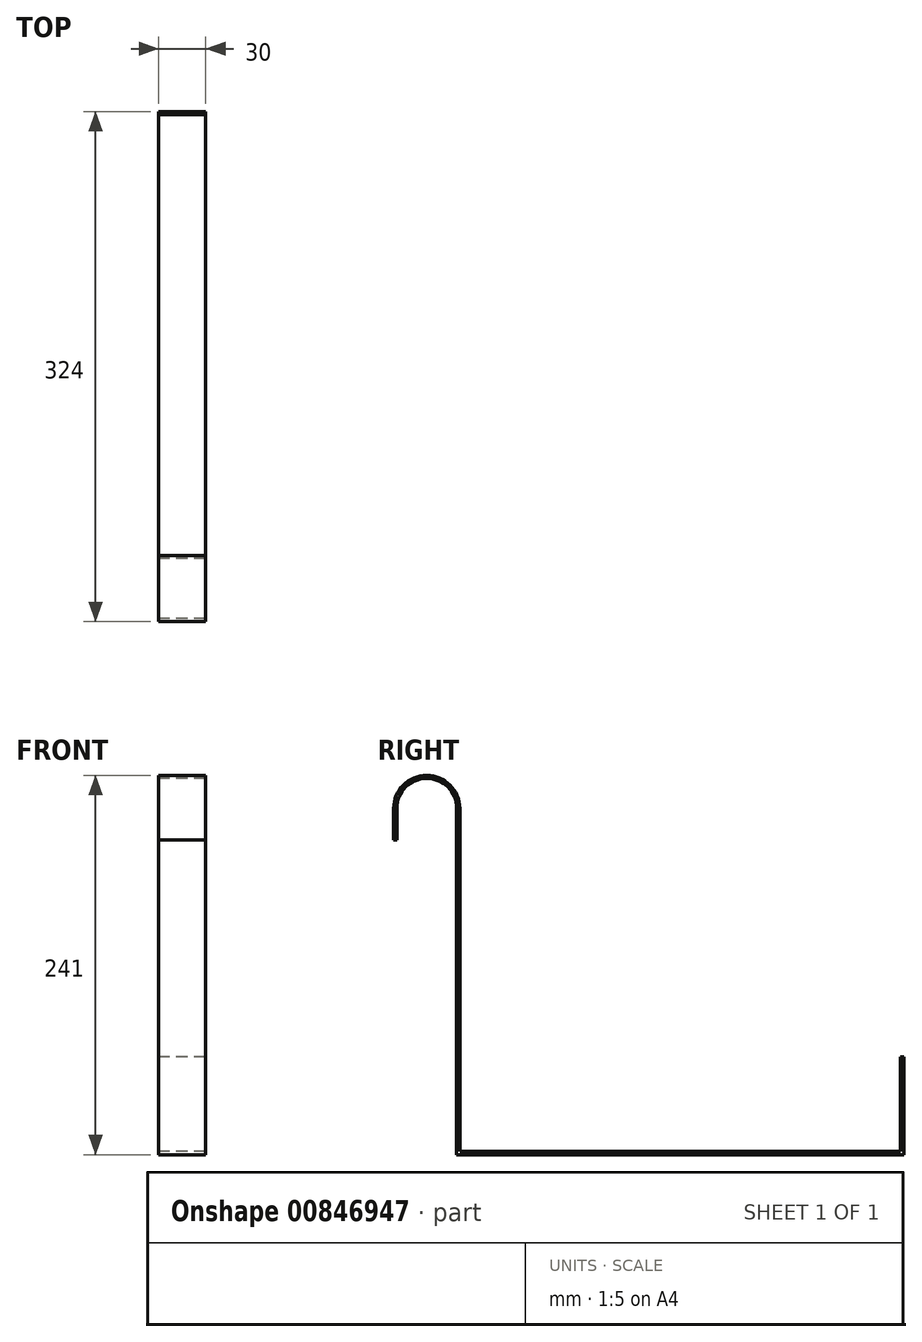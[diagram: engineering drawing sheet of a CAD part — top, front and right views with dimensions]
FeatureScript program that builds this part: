
annotation { "Feature Type Name" : "Feature", "Feature Type Description" : "" }
export const myFeature = defineFeature(function(context is Context, id is Id, definition is map)
    precondition{}
    {
        {
            var Q0;
            Q0=qCreatedBy(makeId("Right.planeOp"),FACE);
            var sketch = newSketch(context, id + "F0", { "sketchPlane" : qUnion([Q0])});
            skArc(sketch, "E0", {"start": v(19, 220) * mm, "mid": v(0, 239) * mm, "end": v(-19, 220) * mm});
            skLineSegment(sketch, "E1", {"start": v(0, 220) * mm, "end": v(19, 220) * mm, "construction": true});
            skLineSegment(sketch, "E2", {"start": v(19, 220) * mm, "end": v(19, 0) * mm});
            skLineSegment(sketch, "E3", {"start": v(0, 220) * mm, "end": v(-19, 220) * mm, "construction": true});
            skArc(sketch, "E4.0", {"start": v(21, 220) * mm, "mid": v(0, 241) * mm, "end": v(-21, 220) * mm});
            skLineSegment(sketch, "E4.1", {"start": v(21, 220) * mm, "end": v(21, 0) * mm});
            skLineSegment(sketch, "E5", {"start": v(21, 0) * mm, "end": v(19, 0) * mm});
            skLineSegment(sketch, "E6", {"start": v(-19, 220) * mm, "end": v(-19, 200) * mm});
            skLineSegment(sketch, "E7", {"start": v(-19, 200) * mm, "end": v(-21, 200) * mm});
            skLineSegment(sketch, "E8", {"start": v(-21, 200) * mm, "end": v(-21, 220) * mm});
            skSolve(sketch);
        }
        {
            var Q0;
            Q0 = qSketchRegion(id + "F0", true);
            extrude(context, id + "F1", {"entities" : qUnion([Q0]), "depth" : 30 * mm, "offsetDistance" : 25 * mm});
        }
        {
            var Q0;
            Q0=makeQuery(id+"F1.opExtrude","SWEPT_FACE",FACE,{"disambiguationData":[OSD([sQuery(id+"F0.wireOp",EDGE,"E4.1")])]});
            var sketch = newSketch(context, id + "F2", { "sketchPlane" : qUnion([Q0])});
            skLineSegment(sketch, "E9.bottom", {"start": v(-30, 0) * mm, "end": v(0, 0) * mm});
            skLineSegment(sketch, "E9.top", {"start": v(-30, 2) * mm, "end": v(0, 2) * mm});
            skLineSegment(sketch, "E9.left", {"start": v(-30, 0) * mm, "end": v(-30, 2) * mm});
            skLineSegment(sketch, "E9.right", {"start": v(0, 0) * mm, "end": v(0, 2) * mm});
            skSolve(sketch);
        }
        {
            var Q0;
            Q0 = qSketchRegion(id + "F2", true);
            extrude(context, id + "F3", {"entities" : qUnion([Q0]), "operationType" : NewBodyOperationType.ADD, "depth" : 280 * mm, "offsetDistance" : 25 * mm});
        }
        {
            var Q0;
            Q0=makeQuery(id+"F3.opExtrude","SWEPT_FACE",FACE,{"disambiguationData":[OSD([sQuery(id+"F2.wireOp",EDGE,"E9.top")])]});
            var sketch = newSketch(context, id + "F4", { "sketchPlane" : qUnion([Q0])});
            skLineSegment(sketch, "E10.bottom", {"start": v(0, 301) * mm, "end": v(30, 301) * mm});
            skLineSegment(sketch, "E10.top", {"start": v(0, 303) * mm, "end": v(30, 303) * mm});
            skLineSegment(sketch, "E10.left", {"start": v(0, 303) * mm, "end": v(0, 301) * mm});
            skLineSegment(sketch, "E10.right", {"start": v(30, 303) * mm, "end": v(30, 301) * mm});
            skSolve(sketch);
        }
        {
            var Q0;
            Q0=makeQuery(id+"F4.imprint","IMPRINT",FACE,{"disambiguationData":[TD([[makeQuery(id+"F4.imprint","IMPRINT",EDGE,{"derivedFrom":sQuery(id+"F4.wireOp",EDGE,"E10.bottom")}),-1.0]])]});
            extrude(context, id + "F5", {"entities" : qUnion([Q0]), "operationType" : NewBodyOperationType.ADD, "depth" : 60 * mm, "offsetDistance" : 25 * mm, "hasSecondDirection" : true, "secondDirectionOppositeDirection" : true, "secondDirectionDepth" : 2 * mm});
        }
    });
